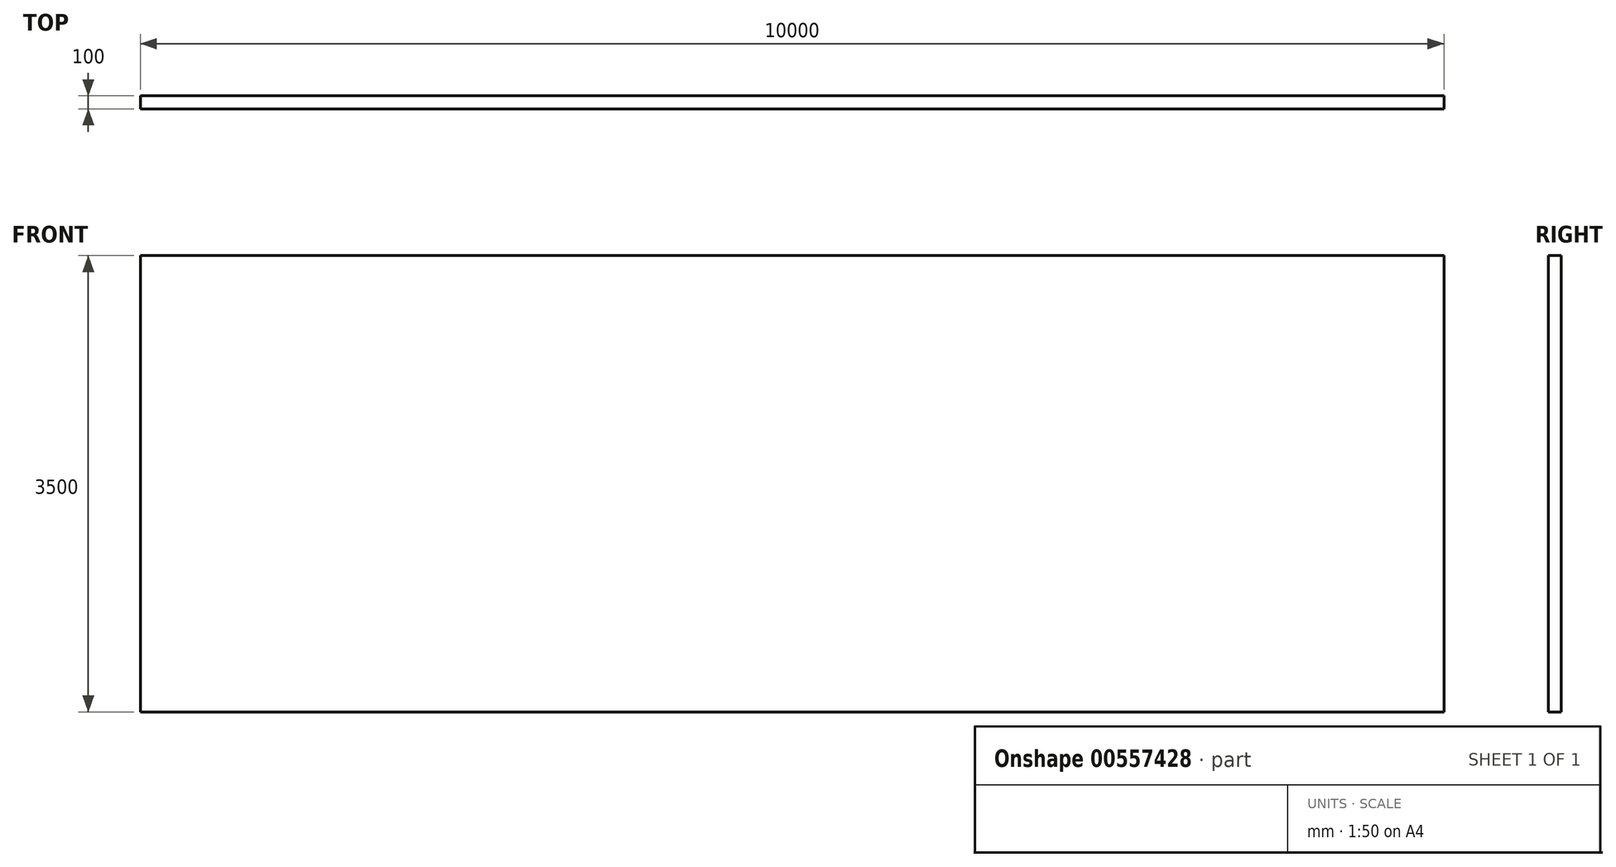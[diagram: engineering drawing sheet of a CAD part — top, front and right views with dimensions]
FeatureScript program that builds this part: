
annotation { "Feature Type Name" : "Feature", "Feature Type Description" : "" }
export const myFeature = defineFeature(function(context is Context, id is Id, definition is map)
    precondition{}
    {
        {
            var Q0;
            Q0=qCreatedBy(makeId("Front.planeOp"),FACE);
            var sketch = newSketch(context, id + "F0", { "sketchPlane" : qUnion([Q0])});
            skLineSegment(sketch, "E0.bottom", {"start": v(5000, 1750) * mm, "end": v(-5000, 1750) * mm});
            skLineSegment(sketch, "E0.top", {"start": v(5000, -1750) * mm, "end": v(-5000, -1750) * mm});
            skLineSegment(sketch, "E0.left", {"start": v(5000, 1750) * mm, "end": v(5000, -1750) * mm});
            skLineSegment(sketch, "E0.right", {"start": v(-5000, 1750) * mm, "end": v(-5000, -1750) * mm});
            skPoint(sketch, "E0.middle", {"position": v(0, 0) * mm});
            skSolve(sketch);
        }
        {
            var Q0;
            Q0=makeQuery(id+"F0.imprint","IMPRINT",FACE,{"disambiguationData":[TD([[makeQuery(id+"F0.imprint","IMPRINT",EDGE,{"derivedFrom":sQuery(id+"F0.wireOp",EDGE,"E0.bottom")}),1.0]])]});
            extrude(context, id + "F1", {"entities" : qUnion([Q0]), "endBound" : BoundingType.SYMMETRIC, "depth" : 100 * mm, "offsetDistance" : 25 * mm});
        }
    });
